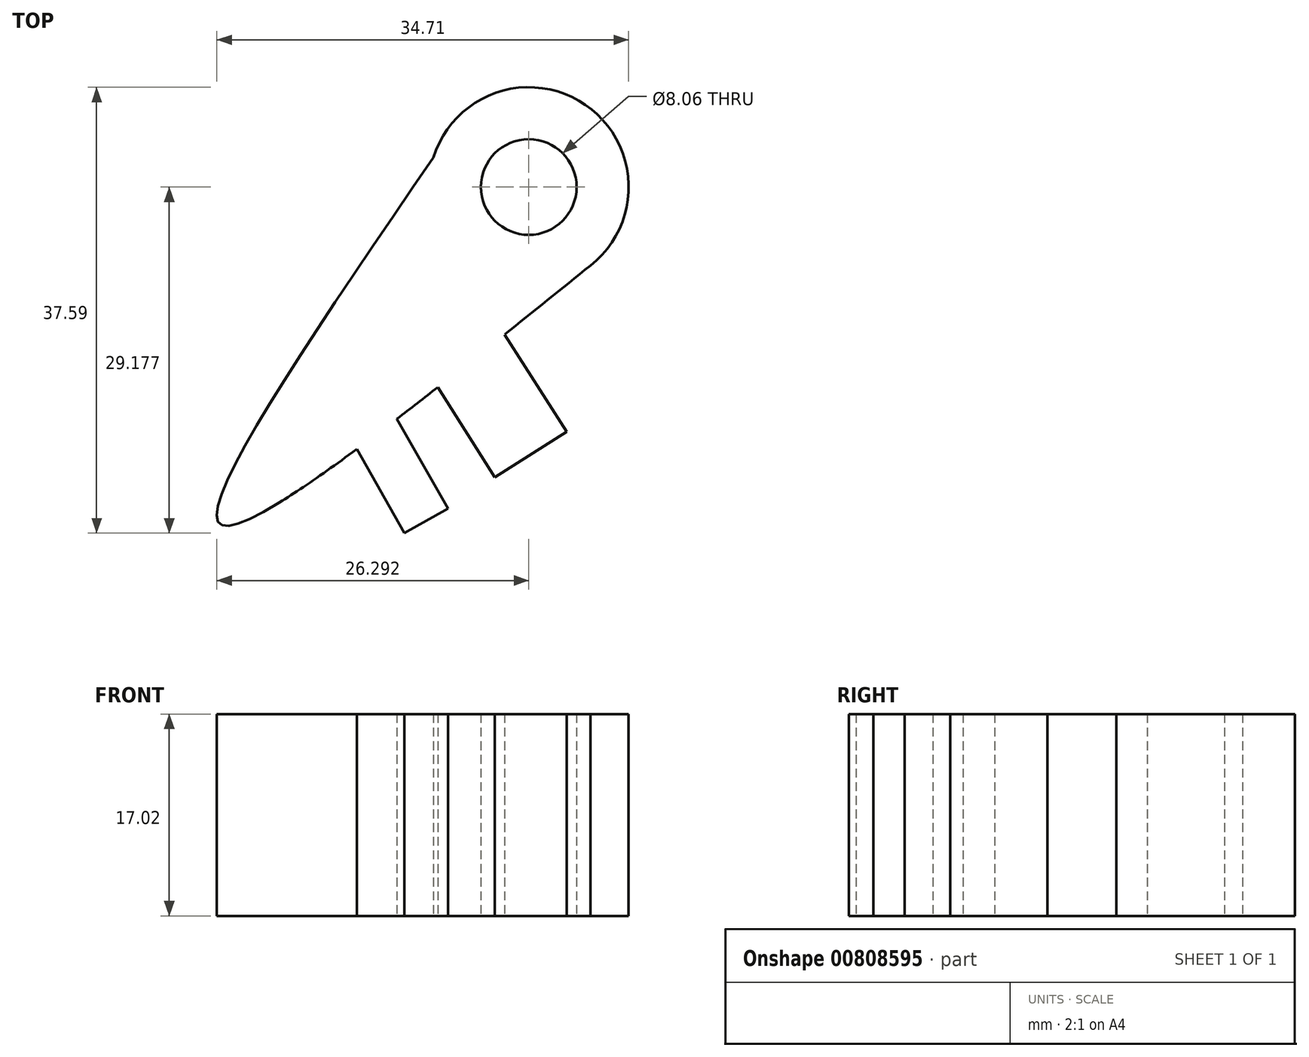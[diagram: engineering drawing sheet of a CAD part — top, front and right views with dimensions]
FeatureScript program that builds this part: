
annotation { "Feature Type Name" : "Feature", "Feature Type Description" : "" }
export const myFeature = defineFeature(function(context is Context, id is Id, definition is map)
    precondition{}
    {
        {
            var Q0;
            Q0=qCreatedBy(makeId("Top.planeOp"),FACE);
            var sketch = newSketch(context, id + "F0", { "sketchPlane" : qUnion([Q0])});
            skCircle(sketch, "E0", {"center": v(38.7, 37.45) * mm, "radius": 8.42 * mm});
            skCircle(sketch, "E1", {"center": v(38.7, 37.45) * mm, "radius": 4.03 * mm});
            skFitSpline(sketch, "E2", {"points": [v(30.66, 39.94) * mm, v(12.64, 9.07) * mm, v(43.9, 30.83) * mm], "startDerivative": vector(-60.8, -88.68) * mm, "endDerivative": vector(86.53, 69.58) * mm});
            skLineSegment(sketch, "E3", {"start": v(24.2, 15.35) * mm, "end": v(28.23, 8.27) * mm});
            skLineSegment(sketch, "E4", {"start": v(28.23, 8.27) * mm, "end": v(31.89, 10.35) * mm});
            skLineSegment(sketch, "E5", {"start": v(31.89, 10.35) * mm, "end": v(27.6, 17.9) * mm});
            skLineSegment(sketch, "E6", {"start": v(31.03, 20.57) * mm, "end": v(35.83, 12.99) * mm});
            skLineSegment(sketch, "E7", {"start": v(35.83, 12.99) * mm, "end": v(41.9, 16.83) * mm});
            skLineSegment(sketch, "E8", {"start": v(41.9, 16.83) * mm, "end": v(36.66, 25.02) * mm});
            skLineSegment(sketch, "E9", {"start": v(17.67, 10.85) * mm, "end": v(20.2, 5.8) * mm});
            skLineSegment(sketch, "E10", {"start": v(20.2, 5.8) * mm, "end": v(20.2, 8.58) * mm});
            skLineSegment(sketch, "E11", {"start": v(20.2, 8.58) * mm, "end": v(23.98, 5.8) * mm});
            skLineSegment(sketch, "E12", {"start": v(23.98, 5.8) * mm, "end": v(20.2, 11.79) * mm});
            skPoint(sketch, "E13.firstSnap0", {"position": v(39.29, 20.93) * mm});
            skLineSegment(sketch, "E13.bottom", {"start": v(20.69, 20.93) * mm, "end": v(27.6, 20.93) * mm});
            skLineSegment(sketch, "E13.top", {"start": v(20.69, 17.9) * mm, "end": v(27.6, 17.9) * mm});
            skLineSegment(sketch, "E13.left", {"start": v(20.69, 20.93) * mm, "end": v(20.69, 17.9) * mm});
            skLineSegment(sketch, "E13.right", {"start": v(27.6, 20.93) * mm, "end": v(27.6, 17.9) * mm});
            skSolve(sketch);
        }
        {
            var Q0;
            Q0=makeQuery(id+"F0.imprint","IMPRINT",FACE,{"disambiguationData":[TD([[makeQuery(id+"F0.imprint","IMPRINT",EDGE,{"derivedFrom":sQuery(id+"F0.wireOp",EDGE,"E0")}),1.0]])]});
            extrude(context, id + "F1", {"entities" : qUnion([Q0]), "depth" : 3.3 * mm, "offsetDistance" : 25.4 * mm});
        }
        {
            var Q0;
            Q0 = qSketchRegion(id + "F0", true);
            extrude(context, id + "F2", {"entities" : qUnion([Q0]), "operationType" : NewBodyOperationType.ADD, "depth" : 8.38 * mm, "offsetDistance" : 25.4 * mm});
        }
        {
            var Q0;
            Q0 = qSketchRegion(id + "F0", true);
            extrude(context, id + "F3", {"entities" : qUnion([Q0]), "operationType" : NewBodyOperationType.ADD, "depth" : 8.64 * mm, "offsetDistance" : 25.4 * mm});
        }
        {
            var Q0;
            Q0 = qSketchRegion(id + "F0", true);
            var Q1;
            Q1=makeQuery(id+"F3.opExtrude","CAP_FACE",FACE,{"disambiguationData":[OSD([sQuery(id+"F0.wireOp",EDGE,"E0"),sQuery(id+"F0.wireOp",EDGE,"E1"),sQuery(id+"F0.wireOp",EDGE,"E2"),sQuery(id+"F0.wireOp",EDGE,"E3"),sQuery(id+"F0.wireOp",EDGE,"E4"),sQuery(id+"F0.wireOp",EDGE,"E5"),sQuery(id+"F0.wireOp",EDGE,"E6"),sQuery(id+"F0.wireOp",EDGE,"E7"),sQuery(id+"F0.wireOp",EDGE,"E8")])],"isStart":false});
            extrude(context, id + "F4", {"entities" : qUnion([Q0, Q1]), "operationType" : NewBodyOperationType.ADD, "depth" : 8.38 * mm, "offsetDistance" : 25.4 * mm});
        }
    });
